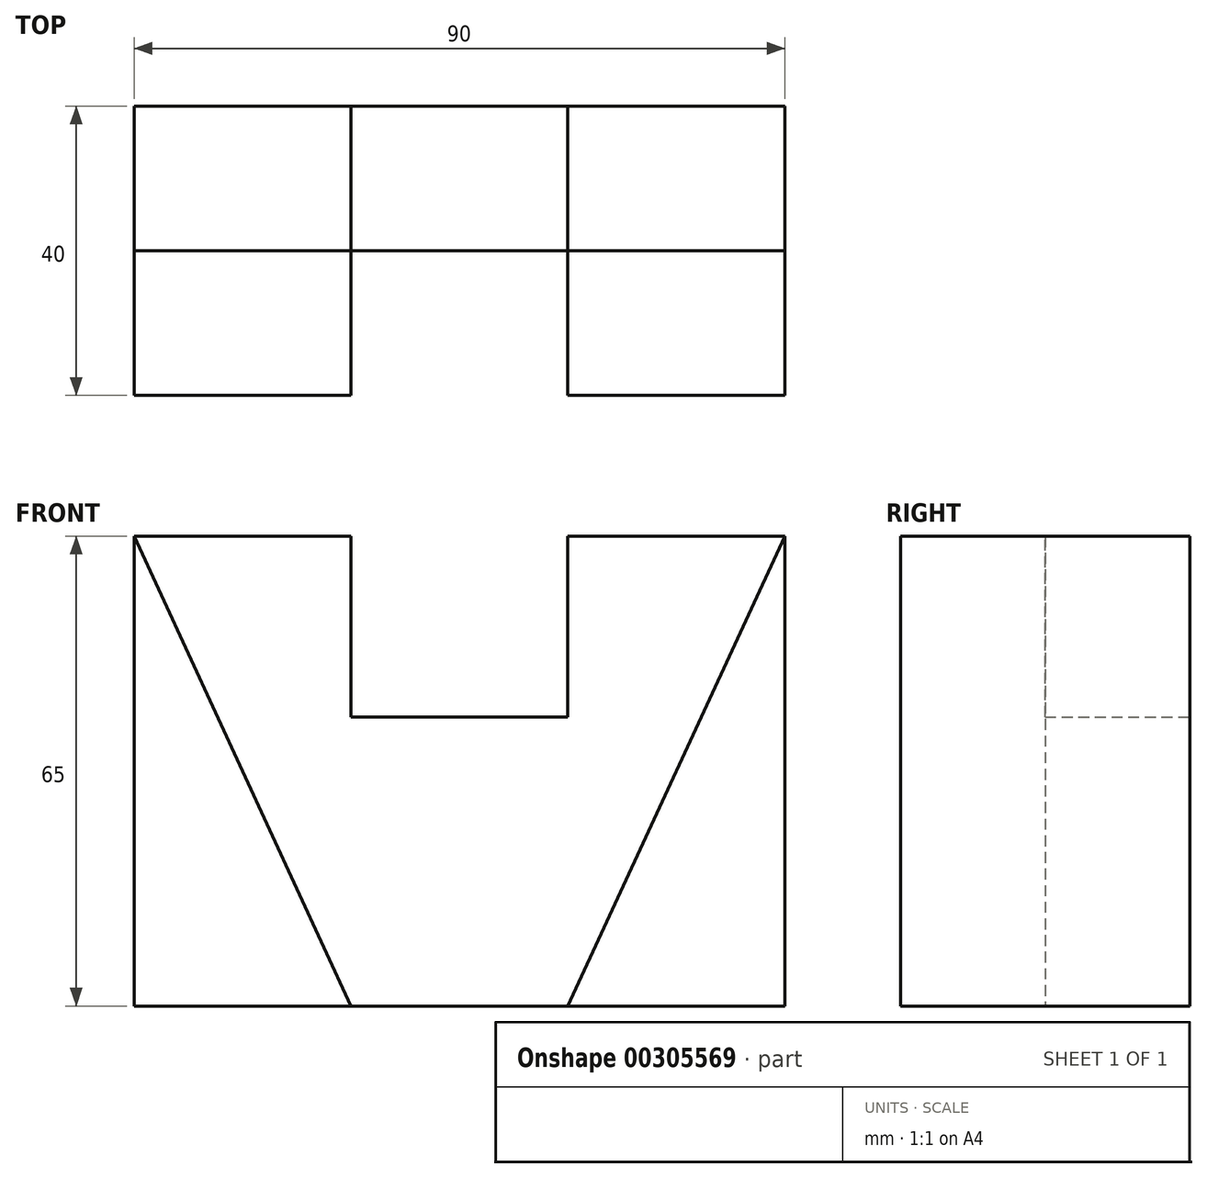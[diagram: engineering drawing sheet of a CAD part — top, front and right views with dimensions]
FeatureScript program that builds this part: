
annotation { "Feature Type Name" : "Feature", "Feature Type Description" : "" }
export const myFeature = defineFeature(function(context is Context, id is Id, definition is map)
    precondition{}
    {
        {
            var Q0;
            Q0=qCreatedBy(makeId("Top.planeOp"),FACE);
            var sketch = newSketch(context, id + "F0", { "sketchPlane" : qUnion([Q0])});
            skLineSegment(sketch, "E0.bottom", {"start": v(-61.22, -14.95) * mm, "end": v(28.78, -14.95) * mm});
            skLineSegment(sketch, "E0.top", {"start": v(-61.22, -54.95) * mm, "end": v(28.78, -54.95) * mm});
            skLineSegment(sketch, "E0.left", {"start": v(-61.22, -14.95) * mm, "end": v(-61.22, -54.95) * mm});
            skLineSegment(sketch, "E0.right", {"start": v(28.78, -14.95) * mm, "end": v(28.78, -54.95) * mm});
            skSolve(sketch);
        }
        {
            var Q0;
            Q0=makeQuery(id+"F0.imprint","IMPRINT",FACE,{"disambiguationData":[TD([[makeQuery(id+"F0.imprint","IMPRINT",EDGE,{"derivedFrom":sQuery(id+"F0.wireOp",EDGE,"E0.bottom")}),-1.0]])]});
            extrude(context, id + "F1", {"entities" : qUnion([Q0]), "depth" : 65 * mm});
        }
        {
            var Q0;
            Q0=makeQuery(id+"F1.opExtrude","CAP_FACE",FACE,{"disambiguationData":[OSD([sQuery(id+"F0.wireOp",EDGE,"E0.bottom"),sQuery(id+"F0.wireOp",EDGE,"E0.top"),sQuery(id+"F0.wireOp",EDGE,"E0.left"),sQuery(id+"F0.wireOp",EDGE,"E0.right")])],"isStart":false});
            var sketch = newSketch(context, id + "F2", { "sketchPlane" : qUnion([Q0])});
            skLineSegment(sketch, "E1", {"start": v(-61.22, -34.95) * mm, "end": v(-31.22, -34.95) * mm});
            skLineSegment(sketch, "E2", {"start": v(-31.22, -34.95) * mm, "end": v(-1.22, -34.95) * mm});
            skLineSegment(sketch, "E3", {"start": v(-1.22, -34.95) * mm, "end": v(28.78, -34.95) * mm});
            skLineSegment(sketch, "E4", {"start": v(-31.22, -34.95) * mm, "end": v(-31.22, -14.95) * mm});
            skLineSegment(sketch, "E5", {"start": v(-1.22, -34.95) * mm, "end": v(-1.22, -14.95) * mm});
            skSolve(sketch);
        }
        {
            var Q0;
            Q0=makeQuery(id+"F2.imprint","IMPRINT",FACE,{"disambiguationData":[TD([[makeQuery(id+"F2.imprint","IMPRINT",EDGE,{"derivedFrom":sQuery(id+"F2.wireOp",EDGE,"E2")}),1.0]])]});
            extrude(context, id + "F3", {"entities" : qUnion([Q0]), "operationType" : NewBodyOperationType.REMOVE, "oppositeDirection" : true, "depth" : 25 * mm});
        }
        {
            var Q0;
            Q0=makeQuery(id+"F1.opExtrude","SWEPT_FACE",FACE,{"disambiguationData":[OSD([sQuery(id+"F0.wireOp",EDGE,"E0.top")])]});
            var sketch = newSketch(context, id + "F4", { "sketchPlane" : qUnion([Q0])});
            skLineSegment(sketch, "E6", {"start": v(-61.22, 0) * mm, "end": v(-31.22, 0) * mm});
            skLineSegment(sketch, "E7", {"start": v(-31.22, 0) * mm, "end": v(-1.22, 0) * mm});
            skLineSegment(sketch, "E8", {"start": v(-1.22, 0) * mm, "end": v(28.78, 0) * mm});
            skLineSegment(sketch, "E9", {"start": v(-61.22, 65) * mm, "end": v(-31.22, 0) * mm});
            skLineSegment(sketch, "E10", {"start": v(28.78, 65) * mm, "end": v(-1.22, 0) * mm});
            skSolve(sketch);
        }
        {
            var Q0;
            Q0=makeQuery(id+"F4.imprint","IMPRINT",FACE,{"disambiguationData":[TD([[makeQuery(id+"F4.imprint","IMPRINT",EDGE,{"derivedFrom":sQuery(id+"F4.wireOp",EDGE,"E7")}),1.0]])]});
            extrude(context, id + "F5", {"entities" : qUnion([Q0]), "operationType" : NewBodyOperationType.REMOVE, "oppositeDirection" : true, "depth" : 20 * mm});
        }
    });
